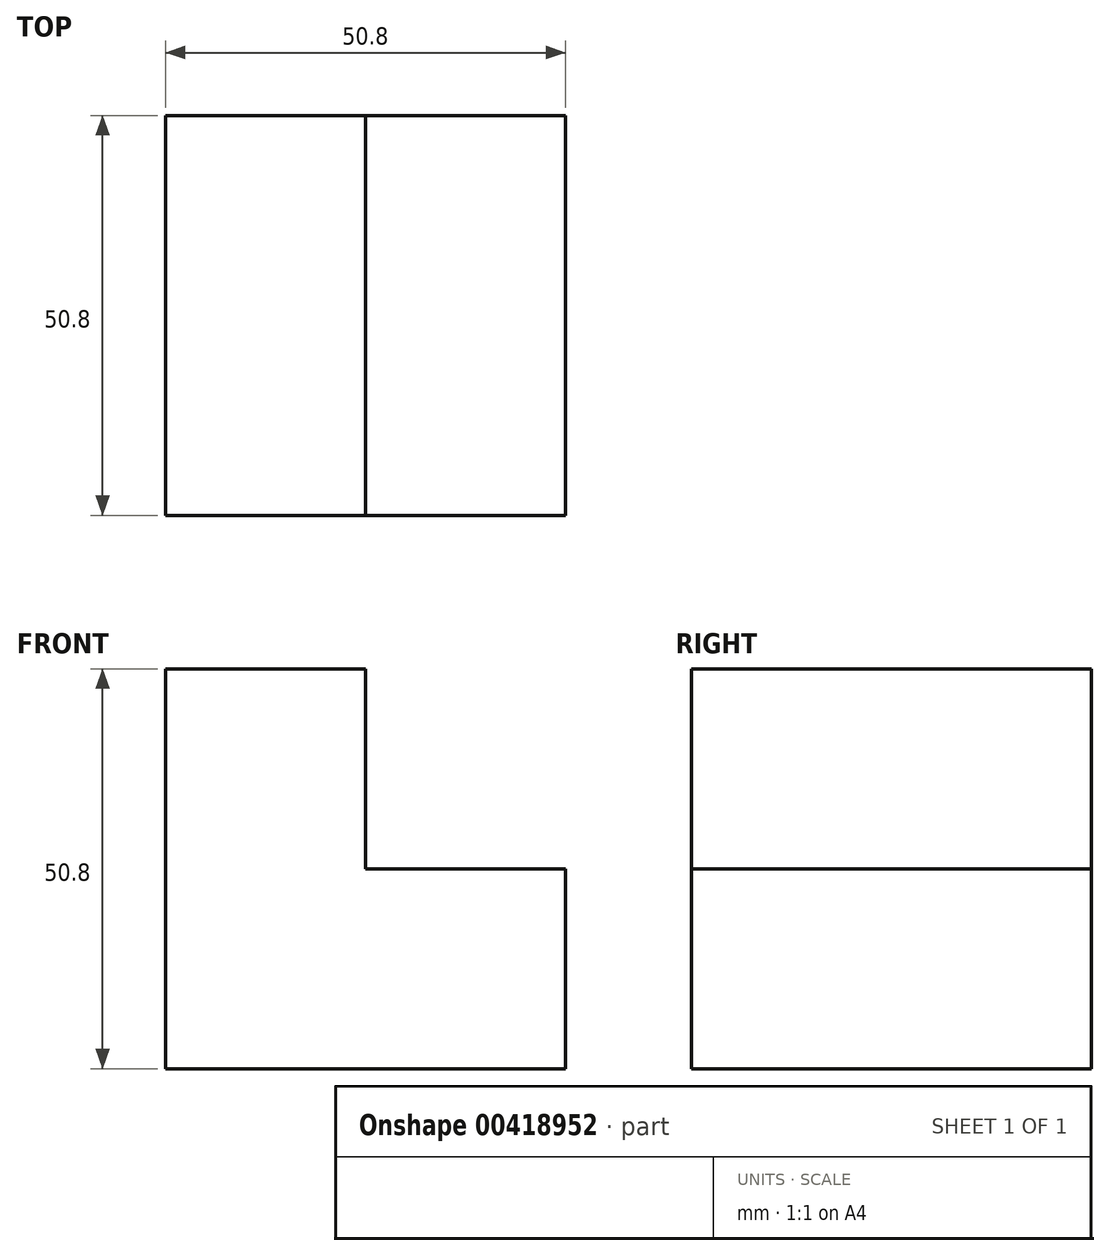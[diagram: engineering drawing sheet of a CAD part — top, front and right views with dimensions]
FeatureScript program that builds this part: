
annotation { "Feature Type Name" : "Feature", "Feature Type Description" : "" }
export const myFeature = defineFeature(function(context is Context, id is Id, definition is map)
    precondition{}
    {
        {
            var Q0;
            Q0=qCreatedBy(makeId("Front.planeOp"),FACE);
            var sketch = newSketch(context, id + "F0", { "sketchPlane" : qUnion([Q0])});
            skLineSegment(sketch, "E0", {"start": v(0, 0) * mm, "end": v(-50.8, 0) * mm});
            skLineSegment(sketch, "E1", {"start": v(-50.8, 50.8) * mm, "end": v(-50.8, 0) * mm});
            skLineSegment(sketch, "E2", {"start": v(-25.4, 50.8) * mm, "end": v(-22.53, 50.8) * mm});
            skLineSegment(sketch, "E3", {"start": v(-25.4, 50.8) * mm, "end": v(-50.8, 50.8) * mm});
            skLineSegment(sketch, "E4", {"start": v(-25.4, 25.4) * mm, "end": v(-25.4, 50.8) * mm});
            skLineSegment(sketch, "E5", {"start": v(-25.4, 25.4) * mm, "end": v(0, 25.4) * mm});
            skLineSegment(sketch, "E6", {"start": v(0, 0) * mm, "end": v(0, 25.4) * mm});
            skSolve(sketch);
        }
        {
            var Q0;
            Q0=makeQuery(id+"F0.imprint","IMPRINT",FACE,{"disambiguationData":[TD([[makeQuery(id+"F0.imprint","IMPRINT",EDGE,{"derivedFrom":sQuery(id+"F0.wireOp",EDGE,"E0")}),-1.0]])]});
            extrude(context, id + "F1", {"entities" : qUnion([Q0]), "depth" : 50.8 * mm});
        }
    });
